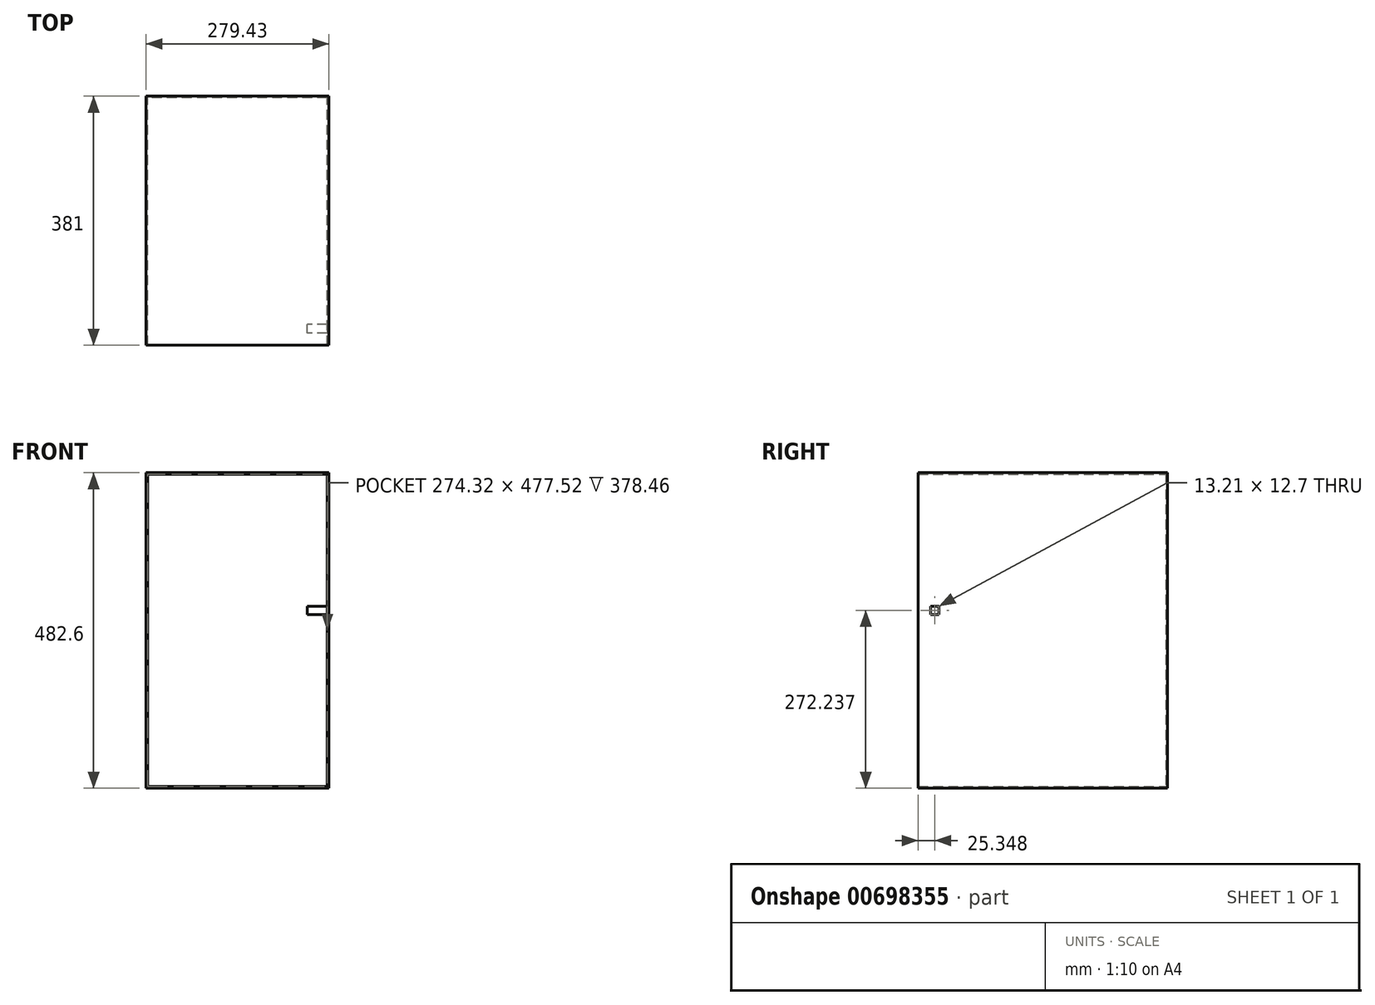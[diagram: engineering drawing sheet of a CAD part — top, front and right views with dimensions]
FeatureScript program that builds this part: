
annotation { "Feature Type Name" : "Feature", "Feature Type Description" : "" }
export const myFeature = defineFeature(function(context is Context, id is Id, definition is map)
    precondition{}
    {
        {
            var Q0;
            Q0=qCreatedBy(makeId("Front.planeOp"),FACE);
            var sketch = newSketch(context, id + "F0", { "sketchPlane" : qUnion([Q0])});
            skLineSegment(sketch, "E0.bottom", {"start": v(139.7, 241.3) * mm, "end": v(-139.7, 241.3) * mm});
            skLineSegment(sketch, "E0.top", {"start": v(139.7, -241.3) * mm, "end": v(-139.7, -241.3) * mm});
            skLineSegment(sketch, "E0.left", {"start": v(139.7, 241.3) * mm, "end": v(139.7, -241.3) * mm});
            skLineSegment(sketch, "E0.right", {"start": v(-139.7, 241.3) * mm, "end": v(-139.7, -241.3) * mm});
            skPoint(sketch, "E0.middle", {"position": v(0, 0) * mm});
            skSolve(sketch);
        }
        {
            var Q0;
            Q0 = qSketchRegion(id + "F0", true);
            extrude(context, id + "F1", {"entities" : qUnion([Q0]), "endBound" : BoundingType.SYMMETRIC, "depth" : 381 * mm, "offsetDistance" : 25.4 * mm});
        }
        {
            var Q0;
            Q0=makeQuery(id+"F1.opExtrude","CAP_FACE",FACE,{"disambiguationData":[OSD([sQuery(id+"F0.wireOp",EDGE,"E0.bottom"),sQuery(id+"F0.wireOp",EDGE,"E0.top"),sQuery(id+"F0.wireOp",EDGE,"E0.left"),sQuery(id+"F0.wireOp",EDGE,"E0.right")])],"isStart":false});
            shell(context, id + "F2", {"entities" : qUnion([Q0]), "thickness" : 2.54 * mm});
        }
        {
            var Q0;
            Q0=makeQuery(id+"F1.opExtrude","SWEPT_FACE",FACE,{"disambiguationData":[OSD([sQuery(id+"F0.wireOp",EDGE,"E0.left")])]});
            var sketch = newSketch(context, id + "F3", { "sketchPlane" : qUnion([Q0])});
            skLineSegment(sketch, "E1", {"start": v(-174.9, 241.3) * mm, "end": v(-174.9, 40.8) * mm});
            skLineSegment(sketch, "E2", {"start": v(-174.9, -241.3) * mm, "end": v(-174.9, -40.49) * mm});
            skLineSegment(sketch, "E3", {"start": v(-174.9, 40.8) * mm, "end": v(-174.9, 37.29) * mm});
            skLineSegment(sketch, "E4", {"start": v(-174.9, 37.29) * mm, "end": v(-171.76, 37.29) * mm});
            skLineSegment(sketch, "E5", {"start": v(-171.76, 37.29) * mm, "end": v(-158.55, 37.29) * mm});
            skLineSegment(sketch, "E6", {"start": v(-158.55, 37.29) * mm, "end": v(-158.55, 24.59) * mm});
            skLineSegment(sketch, "E7.top", {"start": v(-171.76, 24.59) * mm, "end": v(-158.55, 24.59) * mm});
            skLineSegment(sketch, "E7.left", {"start": v(-171.76, 37.29) * mm, "end": v(-171.76, 24.59) * mm});
            skSolve(sketch);
        }
        {
            var Q0;
            Q0=makeQuery(id+"F3.imprint","IMPRINT",FACE,{"disambiguationData":[TD([[makeQuery(id+"F3.imprint","IMPRINT",EDGE,{"derivedFrom":sQuery(id+"F3.wireOp",EDGE,"E5")}),-1.0]])]});
            extrude(context, id + "F4", {"entities" : qUnion([Q0]), "operationType" : NewBodyOperationType.ADD, "depth" : 0.03 * mm, "offsetDistance" : 25.4 * mm, "hasSecondDirection" : true, "secondDirectionOppositeDirection" : true, "secondDirectionDepth" : 33.02 * mm});
        }
    });
